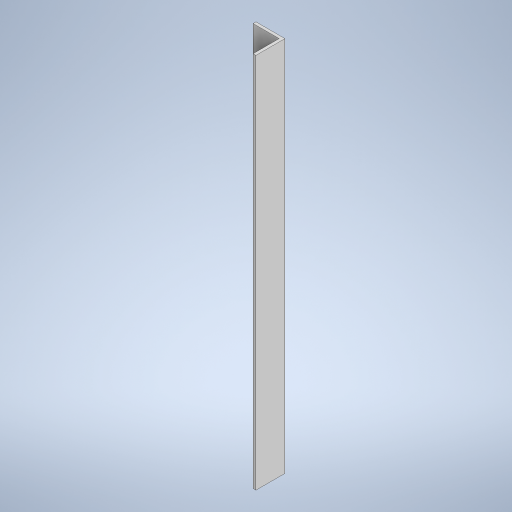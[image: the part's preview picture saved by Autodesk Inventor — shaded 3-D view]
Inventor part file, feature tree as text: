
AUTODESK INVENTOR PART (.ipt)
format: ipt  version: 2024 (Build 280153000, 153)  size: 235,008 bytes
history: native  units: mm
features: extrude x1, sketch x1
ambient origin geometry x8: Origin, YZ Plane, XZ Plane, XY Plane, X Axis, Y Axis, Z Axis, Center Point
bodies: Solid1 (feature_tree)
feature tree (2):
  extrude  "Extrusion1"  Depth=50.0mm
  sketch  "Sketch1"  dims[d2=5.0mm d3=50.0mm d4=50.0mm d5=45.0mm d6=5.0mm d7=650.0mm d8=0.0mm]
